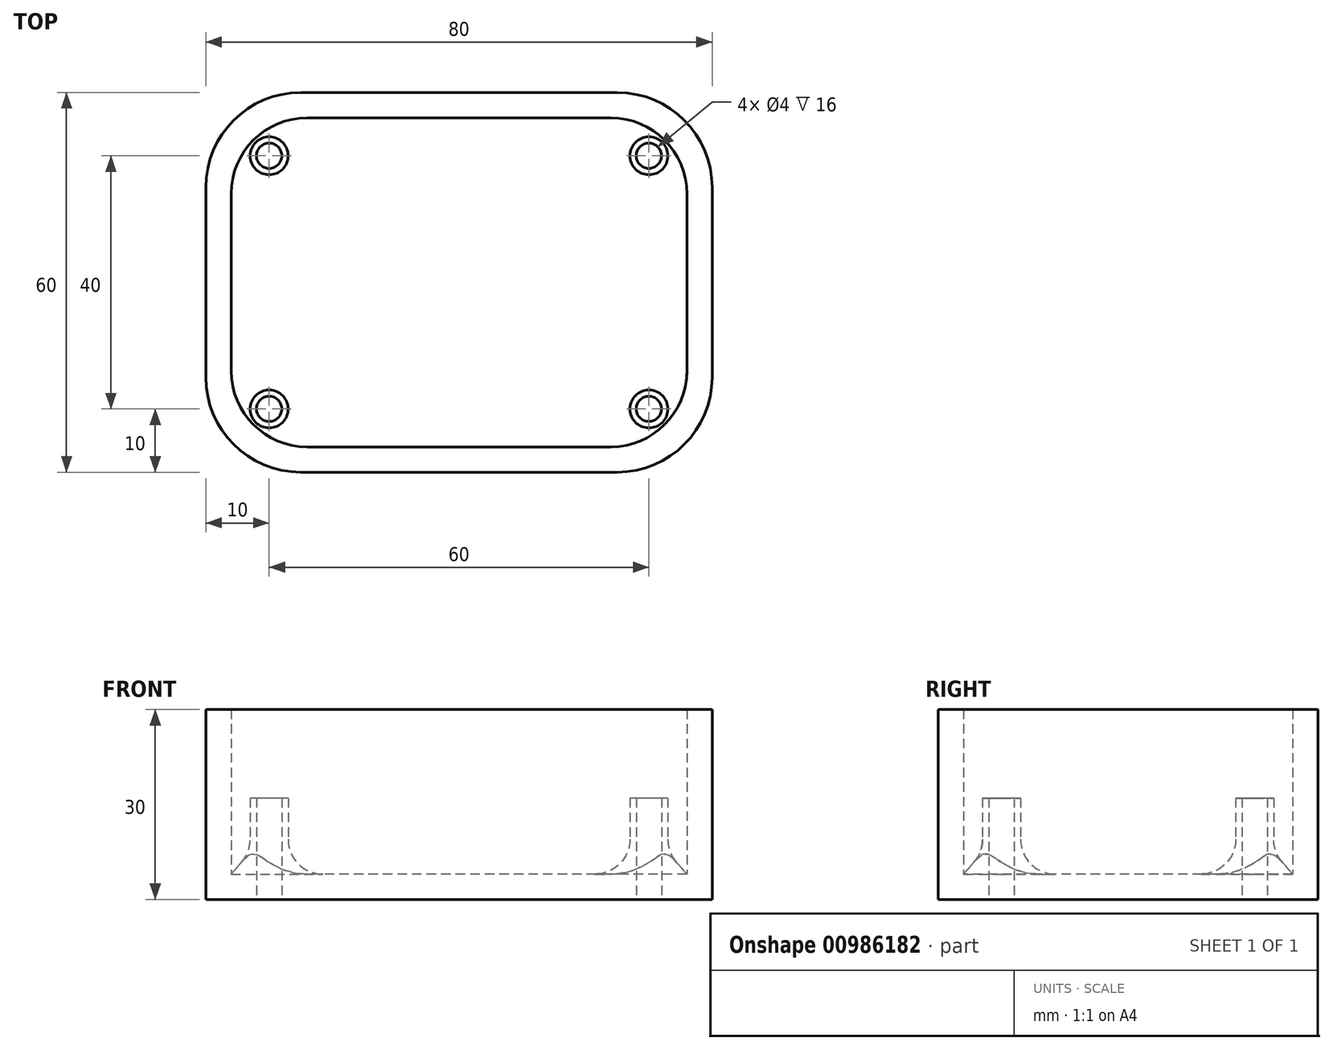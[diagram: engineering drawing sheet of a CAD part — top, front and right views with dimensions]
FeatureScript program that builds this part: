
annotation { "Feature Type Name" : "Feature", "Feature Type Description" : "" }
export const myFeature = defineFeature(function(context is Context, id is Id, definition is map)
    precondition{}
    {
        {
            var Q0;
            Q0=qCreatedBy(makeId("Top.planeOp"),FACE);
            var sketch = newSketch(context, id + "F0", { "sketchPlane" : qUnion([Q0])});
            skLineSegment(sketch, "E0.bottom", {"start": v(40, 30) * mm, "end": v(-40, 30) * mm});
            skLineSegment(sketch, "E0.top", {"start": v(40, -30) * mm, "end": v(-40, -30) * mm});
            skLineSegment(sketch, "E0.left", {"start": v(40, 30) * mm, "end": v(40, -30) * mm});
            skLineSegment(sketch, "E0.right", {"start": v(-40, 30) * mm, "end": v(-40, -30) * mm});
            skPoint(sketch, "E0.middle", {"position": v(0, 0) * mm});
            skLineSegment(sketch, "E1.0", {"start": v(36, 26) * mm, "end": v(-36, 26) * mm});
            skLineSegment(sketch, "E1.1", {"start": v(36, 26) * mm, "end": v(36, -26) * mm});
            skLineSegment(sketch, "E1.2", {"start": v(36, -26) * mm, "end": v(-36, -26) * mm});
            skLineSegment(sketch, "E1.3", {"start": v(-36, 26) * mm, "end": v(-36, -26) * mm});
            skLineSegment(sketch, "E2.0", {"start": v(30, 20) * mm, "end": v(-30, 20) * mm, "construction": true});
            skLineSegment(sketch, "E2.1", {"start": v(30, 20) * mm, "end": v(30, -20) * mm, "construction": true});
            skLineSegment(sketch, "E2.2", {"start": v(30, -20) * mm, "end": v(-30, -20) * mm, "construction": true});
            skLineSegment(sketch, "E2.3", {"start": v(-30, 20) * mm, "end": v(-30, -20) * mm, "construction": true});
            skCircle(sketch, "E3", {"center": v(-30, 20) * mm, "radius": 3 * mm});
            skCircle(sketch, "E4", {"center": v(30, 20) * mm, "radius": 3 * mm});
            skCircle(sketch, "E5", {"center": v(-30, -20) * mm, "radius": 3 * mm});
            skCircle(sketch, "E6", {"center": v(30, -20) * mm, "radius": 3 * mm});
            skCircle(sketch, "E7.0", {"center": v(-30, 20) * mm, "radius": 2 * mm});
            skCircle(sketch, "E8.0", {"center": v(-30, -20) * mm, "radius": 2 * mm});
            skCircle(sketch, "E9.0", {"center": v(30, 20) * mm, "radius": 2 * mm});
            skCircle(sketch, "E10.0", {"center": v(30, -20) * mm, "radius": 2 * mm});
            skSolve(sketch);
        }
        {
            var Q0;
            Q0=makeQuery(id+"F0.imprint","IMPRINT",FACE,{"disambiguationData":[TD([[makeQuery(id+"F0.imprint","IMPRINT",EDGE,{"derivedFrom":sQuery(id+"F0.wireOp",EDGE,"E0.bottom")}),1.0]])]});
            var Q1;
            Q1=makeQuery(id+"F0.imprint","IMPRINT",FACE,{"disambiguationData":[TD([[makeQuery(id+"F0.imprint","IMPRINT",EDGE,{"derivedFrom":sQuery(id+"F0.wireOp",EDGE,"E1.0")}),1.0]])]});
            var Q2;
            Q2=makeQuery(id+"F0.imprint","IMPRINT",FACE,{"disambiguationData":[TD([[makeQuery(id+"F0.imprint","IMPRINT",EDGE,{"derivedFrom":sQuery(id+"F0.wireOp",EDGE,"E3")}),1.0]])]});
            var Q3;
            Q3=makeQuery(id+"F0.imprint","IMPRINT",FACE,{"disambiguationData":[TD([[makeQuery(id+"F0.imprint","IMPRINT",EDGE,{"derivedFrom":sQuery(id+"F0.wireOp",EDGE,"E4")}),1.0]])]});
            var Q4;
            Q4=makeQuery(id+"F0.imprint","IMPRINT",FACE,{"disambiguationData":[TD([[makeQuery(id+"F0.imprint","IMPRINT",EDGE,{"derivedFrom":sQuery(id+"F0.wireOp",EDGE,"E6")}),1.0]])]});
            var Q5;
            Q5=makeQuery(id+"F0.imprint","IMPRINT",FACE,{"disambiguationData":[TD([[makeQuery(id+"F0.imprint","IMPRINT",EDGE,{"derivedFrom":sQuery(id+"F0.wireOp",EDGE,"E5")}),1.0]])]});
            extrude(context, id + "F1", {"entities" : qUnion([Q0, Q1, Q2, Q3, Q4, Q5]), "depth" : 4 * mm, "offsetDistance" : 25 * mm});
        }
        {
            var Q0;
            Q0=makeQuery(id+"F0.imprint","IMPRINT",FACE,{"disambiguationData":[TD([[makeQuery(id+"F0.imprint","IMPRINT",EDGE,{"derivedFrom":sQuery(id+"F0.wireOp",EDGE,"E0.bottom")}),1.0]])]});
            extrude(context, id + "F2", {"entities" : qUnion([Q0]), "depth" : 30 * mm, "offsetDistance" : 25 * mm});
        }
        {
            var Q0;
            Q0=makeQuery(id+"F0.imprint","IMPRINT",FACE,{"disambiguationData":[TD([[makeQuery(id+"F0.imprint","IMPRINT",EDGE,{"derivedFrom":sQuery(id+"F0.wireOp",EDGE,"E3")}),1.0]])]});
            var Q1;
            Q1=makeQuery(id+"F0.imprint","IMPRINT",FACE,{"disambiguationData":[TD([[makeQuery(id+"F0.imprint","IMPRINT",EDGE,{"derivedFrom":sQuery(id+"F0.wireOp",EDGE,"E5")}),1.0]])]});
            var Q2;
            Q2=makeQuery(id+"F0.imprint","IMPRINT",FACE,{"disambiguationData":[TD([[makeQuery(id+"F0.imprint","IMPRINT",EDGE,{"derivedFrom":sQuery(id+"F0.wireOp",EDGE,"E4")}),1.0]])]});
            var Q3;
            Q3=makeQuery(id+"F0.imprint","IMPRINT",FACE,{"disambiguationData":[TD([[makeQuery(id+"F0.imprint","IMPRINT",EDGE,{"derivedFrom":sQuery(id+"F0.wireOp",EDGE,"E6")}),1.0]])]});
            extrude(context, id + "F3", {"entities" : qUnion([Q0, Q1, Q2, Q3]), "depth" : 16 * mm, "offsetDistance" : 25 * mm});
        }
        {
            var Q0;
            Q0=makeQuery(id+"F3.opExtrude","SWEPT_BODY",BODY,{"disambiguationData":[OSD([sQuery(id+"F0.wireOp",EDGE,"E3"),sQuery(id+"F0.wireOp",EDGE,"E7.0")])]});
            var Q1;
            Q1=makeQuery(id+"F3.opExtrude","SWEPT_BODY",BODY,{"disambiguationData":[OSD([sQuery(id+"F0.wireOp",EDGE,"E4"),sQuery(id+"F0.wireOp",EDGE,"E9.0")])]});
            var Q2;
            Q2=makeQuery(id+"F3.opExtrude","SWEPT_BODY",BODY,{"disambiguationData":[OSD([sQuery(id+"F0.wireOp",EDGE,"E6"),sQuery(id+"F0.wireOp",EDGE,"E10.0")])]});
            var Q3;
            Q3=makeQuery(id+"F3.opExtrude","SWEPT_BODY",BODY,{"disambiguationData":[OSD([sQuery(id+"F0.wireOp",EDGE,"E5"),sQuery(id+"F0.wireOp",EDGE,"E8.0")])]});
            var Q4;
            Q4=makeQuery(id+"F2.opExtrude","SWEPT_BODY",BODY,{"disambiguationData":[OSD([sQuery(id+"F0.wireOp",EDGE,"E0.bottom"),sQuery(id+"F0.wireOp",EDGE,"E0.top"),sQuery(id+"F0.wireOp",EDGE,"E0.left"),sQuery(id+"F0.wireOp",EDGE,"E0.right"),sQuery(id+"F0.wireOp",EDGE,"E1.0"),sQuery(id+"F0.wireOp",EDGE,"E1.1"),sQuery(id+"F0.wireOp",EDGE,"E1.2"),sQuery(id+"F0.wireOp",EDGE,"E1.3")])]});
            var Q5;
            Q5=makeQuery(id+"F1.opExtrude","SWEPT_BODY",BODY,{"disambiguationData":[OSD([sQuery(id+"F0.wireOp",EDGE,"E0.bottom"),sQuery(id+"F0.wireOp",EDGE,"E0.top"),sQuery(id+"F0.wireOp",EDGE,"E0.left"),sQuery(id+"F0.wireOp",EDGE,"E0.right"),sQuery(id+"F0.wireOp",EDGE,"E7.0"),sQuery(id+"F0.wireOp",EDGE,"E8.0"),sQuery(id+"F0.wireOp",EDGE,"E9.0"),sQuery(id+"F0.wireOp",EDGE,"E10.0")])]});
            booleanBodies(context, id + "F4", {"operationType" : BooleanOperationType.UNION, "tools" : qUnion([Q0, Q1, Q2, Q3, Q4, Q5])});
        }
        {
            var Q0;
            Q0=makeQuery(id+"F2.opExtrude","SWEPT_EDGE",EDGE,{"disambiguationData":[OSD([sQuery(id+"F0.wireOp",EDGE,"E1.0"),sQuery(id+"F0.wireOp",EDGE,"E1.3")])]});
            var Q1;
            Q1=makeQuery(id+"F2.opExtrude","SWEPT_EDGE",EDGE,{"disambiguationData":[OSD([sQuery(id+"F0.wireOp",EDGE,"E1.0"),sQuery(id+"F0.wireOp",EDGE,"E1.1")])]});
            var Q2;
            Q2=makeQuery(id+"F2.opExtrude","SWEPT_EDGE",EDGE,{"disambiguationData":[OSD([sQuery(id+"F0.wireOp",EDGE,"E1.2"),sQuery(id+"F0.wireOp",EDGE,"E1.3")])]});
            var Q3;
            Q3=makeQuery(id+"F2.opExtrude","SWEPT_EDGE",EDGE,{"disambiguationData":[OSD([sQuery(id+"F0.wireOp",EDGE,"E1.1"),sQuery(id+"F0.wireOp",EDGE,"E1.2")])]});
            fillet(context, id + "F5", {"entities" : qUnion([Q0, Q1, Q2, Q3]), "radius" : 12 * mm, "tangentPropagation" : true, "allowEdgeOverflow" : false});
        }
        {
            var Q0;
            Q0=makeQuery(id+"F2.opExtrude","SWEPT_EDGE",EDGE,{"disambiguationData":[OSD([sQuery(id+"F0.wireOp",EDGE,"E0.top"),sQuery(id+"F0.wireOp",EDGE,"E0.left")])]});
            var Q1;
            Q1=makeQuery(id+"F2.opExtrude","SWEPT_EDGE",EDGE,{"disambiguationData":[OSD([sQuery(id+"F0.wireOp",EDGE,"E0.top"),sQuery(id+"F0.wireOp",EDGE,"E0.right")])]});
            var Q2;
            Q2=makeQuery(id+"F2.opExtrude","SWEPT_EDGE",EDGE,{"disambiguationData":[OSD([sQuery(id+"F0.wireOp",EDGE,"E0.bottom"),sQuery(id+"F0.wireOp",EDGE,"E0.left")])]});
            var Q3;
            Q3=makeQuery(id+"F2.opExtrude","SWEPT_EDGE",EDGE,{"disambiguationData":[OSD([sQuery(id+"F0.wireOp",EDGE,"E0.bottom"),sQuery(id+"F0.wireOp",EDGE,"E0.right")])]});
            fillet(context, id + "F6", {"entities" : qUnion([Q0, Q1, Q2, Q3]), "radius" : 15 * mm, "tangentPropagation" : true, "allowEdgeOverflow" : false});
        }
        {
            var Q0;
            Q0=makeQuery(id+"F4.opBoolean","INTERSECT",EDGE,{"derivedFrom":[makeQuery(id+"F1.opExtrude","CAP_FACE",FACE,{"disambiguationData":[OSD([sQuery(id+"F0.wireOp",EDGE,"E0.bottom"),sQuery(id+"F0.wireOp",EDGE,"E0.top"),sQuery(id+"F0.wireOp",EDGE,"E0.left"),sQuery(id+"F0.wireOp",EDGE,"E0.right"),sQuery(id+"F0.wireOp",EDGE,"E7.0"),sQuery(id+"F0.wireOp",EDGE,"E8.0"),sQuery(id+"F0.wireOp",EDGE,"E9.0"),sQuery(id+"F0.wireOp",EDGE,"E10.0")])],"isStart":false}),makeQuery(id+"F3.opExtrude","SWEPT_FACE",FACE,{"disambiguationData":[OSD([sQuery(id+"F0.wireOp",EDGE,"E3")])]})]});
            var Q1;
            Q1=makeQuery(id+"F4.opBoolean","INTERSECT",EDGE,{"derivedFrom":[makeQuery(id+"F1.opExtrude","CAP_FACE",FACE,{"disambiguationData":[OSD([sQuery(id+"F0.wireOp",EDGE,"E0.bottom"),sQuery(id+"F0.wireOp",EDGE,"E0.top"),sQuery(id+"F0.wireOp",EDGE,"E0.left"),sQuery(id+"F0.wireOp",EDGE,"E0.right"),sQuery(id+"F0.wireOp",EDGE,"E7.0"),sQuery(id+"F0.wireOp",EDGE,"E8.0"),sQuery(id+"F0.wireOp",EDGE,"E9.0"),sQuery(id+"F0.wireOp",EDGE,"E10.0")])],"isStart":false}),makeQuery(id+"F3.opExtrude","SWEPT_FACE",FACE,{"disambiguationData":[OSD([sQuery(id+"F0.wireOp",EDGE,"E5")])]})]});
            var Q2;
            Q2=makeQuery(id+"F4.opBoolean","INTERSECT",EDGE,{"derivedFrom":[makeQuery(id+"F1.opExtrude","CAP_FACE",FACE,{"disambiguationData":[OSD([sQuery(id+"F0.wireOp",EDGE,"E0.bottom"),sQuery(id+"F0.wireOp",EDGE,"E0.top"),sQuery(id+"F0.wireOp",EDGE,"E0.left"),sQuery(id+"F0.wireOp",EDGE,"E0.right"),sQuery(id+"F0.wireOp",EDGE,"E7.0"),sQuery(id+"F0.wireOp",EDGE,"E8.0"),sQuery(id+"F0.wireOp",EDGE,"E9.0"),sQuery(id+"F0.wireOp",EDGE,"E10.0")])],"isStart":false}),makeQuery(id+"F3.opExtrude","SWEPT_FACE",FACE,{"disambiguationData":[OSD([sQuery(id+"F0.wireOp",EDGE,"E4")])]})]});
            var Q3;
            Q3=makeQuery(id+"F4.opBoolean","INTERSECT",EDGE,{"derivedFrom":[makeQuery(id+"F1.opExtrude","CAP_FACE",FACE,{"disambiguationData":[OSD([sQuery(id+"F0.wireOp",EDGE,"E0.bottom"),sQuery(id+"F0.wireOp",EDGE,"E0.top"),sQuery(id+"F0.wireOp",EDGE,"E0.left"),sQuery(id+"F0.wireOp",EDGE,"E0.right"),sQuery(id+"F0.wireOp",EDGE,"E7.0"),sQuery(id+"F0.wireOp",EDGE,"E8.0"),sQuery(id+"F0.wireOp",EDGE,"E9.0"),sQuery(id+"F0.wireOp",EDGE,"E10.0")])],"isStart":false}),makeQuery(id+"F3.opExtrude","SWEPT_FACE",FACE,{"disambiguationData":[OSD([sQuery(id+"F0.wireOp",EDGE,"E6")])]})]});
            fillet(context, id + "F7", {"entities" : qUnion([Q0, Q1, Q2, Q3]), "radius" : 5.5 * mm, "tangentPropagation" : true, "allowEdgeOverflow" : false});
        }
    });
